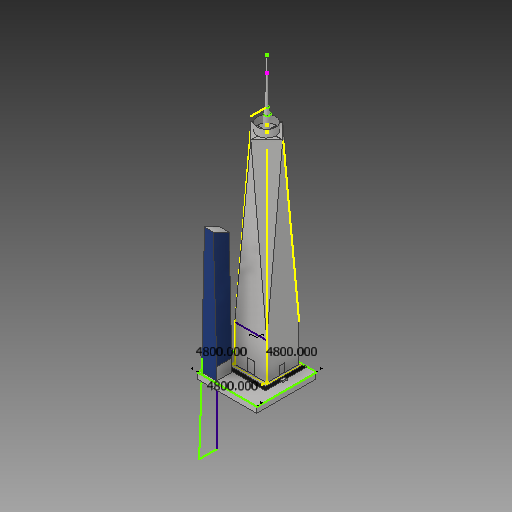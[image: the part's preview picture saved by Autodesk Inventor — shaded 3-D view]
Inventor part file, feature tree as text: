
AUTODESK INVENTOR PART (.ipt)
format: ipt  version: 2018 (Build 220112000, 112)  size: 402,432 bytes
history: native  units: in
note: dims shown in document units (in); Inventor stores cm internally (conversion verified against a paired STEP export)
features: sketch x45, plane x19, extrude x17, other x5, loft x5, fillet x2, projected_geometry x2, delete_face x1
ambient origin geometry x8: Origin, YZ Plane, XZ Plane, XY Plane, X Axis, Y Axis, Z Axis, Center Point
bodies: Solid1 (feature_tree)
feature tree (96):
  other  "Annotations"
  sketch  "Sketch1"  dims[d0=2580.0in d1=2580.0in]
  extrude  "Extrusion1"  Depth=2580.0in
  sketch  "3D Sketch1"
  sketch  "Sketch5"  dims[d31=13416.0in d32=13416.0in]
  sketch  "Sketch6"  dims[d33=90.0deg d34=13416.0in]
  plane  "Work Plane1"
  sketch  "Sketch7"  dims[d35=13416.0in d36=13416.0in]
  plane  "Work Plane2"
  plane  "Work Plane3"
  sketch  "Sketch8"  dims[d37=13416.0in d39=13416.0in]
  sketch  "Sketch9"  dims[d40=0.5805in d41=13416.0in]
  plane  "Work Plane4"
  sketch  "Sketch10"  dims[d42=0.6563in d43=0.0in d44=90.0deg]
  plane  "Work Plane5"
  loft  "Loft1"
  loft  "Loft2"
  extrude  "Extrusion5"  Depth=13416.0in
  sketch  "Sketch13"  dims[d49=0.0in d50=90.0deg d55=1.0in d56=0.0in]
  plane  "Work Plane6"
  extrude  "Extrusion6"  Depth=13416.0in
  plane  "Work Plane7"
  extrude  "Extrusion7"  Depth=13416.0in
  plane  "Work Plane8"
  plane  "Work Plane9"
  sketch  "Sketch16"  dims[d67=1500.0in d68=600.0in d69=0.0in]
  extrude  "Extrusion8"  Depth=13416.0in
  extrude  "Extrusion9"  TaperAngle=0.0deg  [1 undecoded]
  extrude  "Extrusion10"  TaperAngle=0.0deg  [1 undecoded]
  extrude  "Extrusion11"  Depth=1.0in TaperAngle=0.0deg
  delete_face  "Delete Face1"
  extrude  "Extrusion12"  Depth=1.0in TaperAngle=0.0deg
  sketch  "Sketch22"  dims[d88=200.0in d91=200.0in]
  sketch  "Sketch23"  dims[d92=0.0in d93=90.0deg d94=0.0in d95=90.0deg]
  sketch  "Sketch24"  dims[d96=669.0in d97=180.0deg d98=36.0in d99=0.0in]
  sketch  "Sketch25"  dims[d100=36.0in d101=0.0in d102=36.0in d103=0.0in d110=0.0in d111=90.0deg]
  sketch  "Sketch26"  dims[d112=0.0in d113=90.0deg d116=4800.0in]
  fillet  "Fillet1"  Radius=1.0in
  sketch  "Sketch27"  dims[d117=4800.0in d118=4800.0in]
  plane  "Work Plane11"
  loft  "Loft3"
  sketch  "Sketch29"  dims[d124=300.0in]
  extrude  "Extrusion14"  Depth=600.0in TaperAngle=0.0deg
  extrude  "Extrusion15"  Depth=400.0in
  sketch  "Sketch31"  dims[d126=1.0in d127=0.0in]
  extrude  "Extrusion16"  Depth=669.0in
  sketch  "Sketch32"  dims[d128=90.0deg]
  sketch  "Sketch33"  dims[d222=90.0deg]
  plane  "Work Plane12"
  sketch  "Sketch34"  dims[d223=200.0in d224=0.0in]
  loft  "Loft4"
  plane  "Work Plane13"
  sketch  "Sketch35"  dims[d225=200.0in d226=0.0in]
  extrude  "Extrusion19"  Depth=200.0in
  extrude  "Extrusion20"  TaperAngle=0.0deg  [1 undecoded]
  plane  "Work Plane14"
  sketch  "Sketch37"  dims[d228=90.0deg]
  sketch  "Sketch38"  dims[d237=1000.0in d238=0.0in]
  sketch  "Sketch39"  dims[d247=0.0in d248=90.0deg]
  sketch  "Sketch48"  dims[d249=0.0in d250=90.0deg]
  plane  "Work Plane15"
  sketch  "Sketch49"  dims[d114=0.2753in d115=21692.8722in]
  extrude  "Extrusion32"  Depth=36.0in TaperAngle=0.0deg
  extrude  "Extrusion33"  Depth=36.0in TaperAngle=0.0deg
  fillet  "Fillet2"  [1 undecoded]
  plane  "Work Plane16"
  sketch  "Sketch57"
  extrude  "Extrusion37"  Depth=4800.0in
  plane  "Work Plane19"
  sketch  "Sketch59"
  sketch  "Sketch60"
  plane  "Work Plane20"
  sketch  "Sketch61"
  plane  "Work Plane22"
  sketch  "Sketch65"
  plane  "Work Plane23"
  sketch  "Sketch66"
  loft  "Loft7"
  sketch  "Sketch2"  dims[d2=3000.0in d3=0.0in d30=90.0deg]
  sketch  "Sketch12"  dims[d45=0.0in d46=90.0deg d47=0.0in d48=90.0deg]
  sketch  "Sketch14"  dims[d57=1.0in d58=0.0in d59=1.0in d60=0.0in d61=1.0in d62=0.0in]
  sketch  "Sketch15"  dims[d63=1.0in d64=0.0in d65=120.0in d66=0.0in]
  sketch  "Sketch17"  dims[d71=400.0in d72=400.0in]
  sketch  "Sketch18"  dims[d73=1200.0in d74=0.0in d85=669.0in]
  other  "Srf1"
  sketch  "Sketch19"  dims[d86=669.0in d87=180.0deg]
  sketch  "Sketch28"  dims[d119=500.0in d120=0.0in]
  other  "Edges1"
  other  "Edges2"
  sketch  "Sketch36"  dims[d227=111.25in]
  sketch  "Sketch58"
  projected_geometry  "Projected Loop1"
  sketch  "Sketch67"
  sketch  "Sketch30"  dims[d125=300.0in]
  projected_geometry  "Project Cut Edges1"
  other  "Linear Dimension 2"
note: 4 required parameter values undecoded (feature->parameter linkage not recoverable at this tier; creation-order binding heuristic only, values carry confidence <= 0.55)
